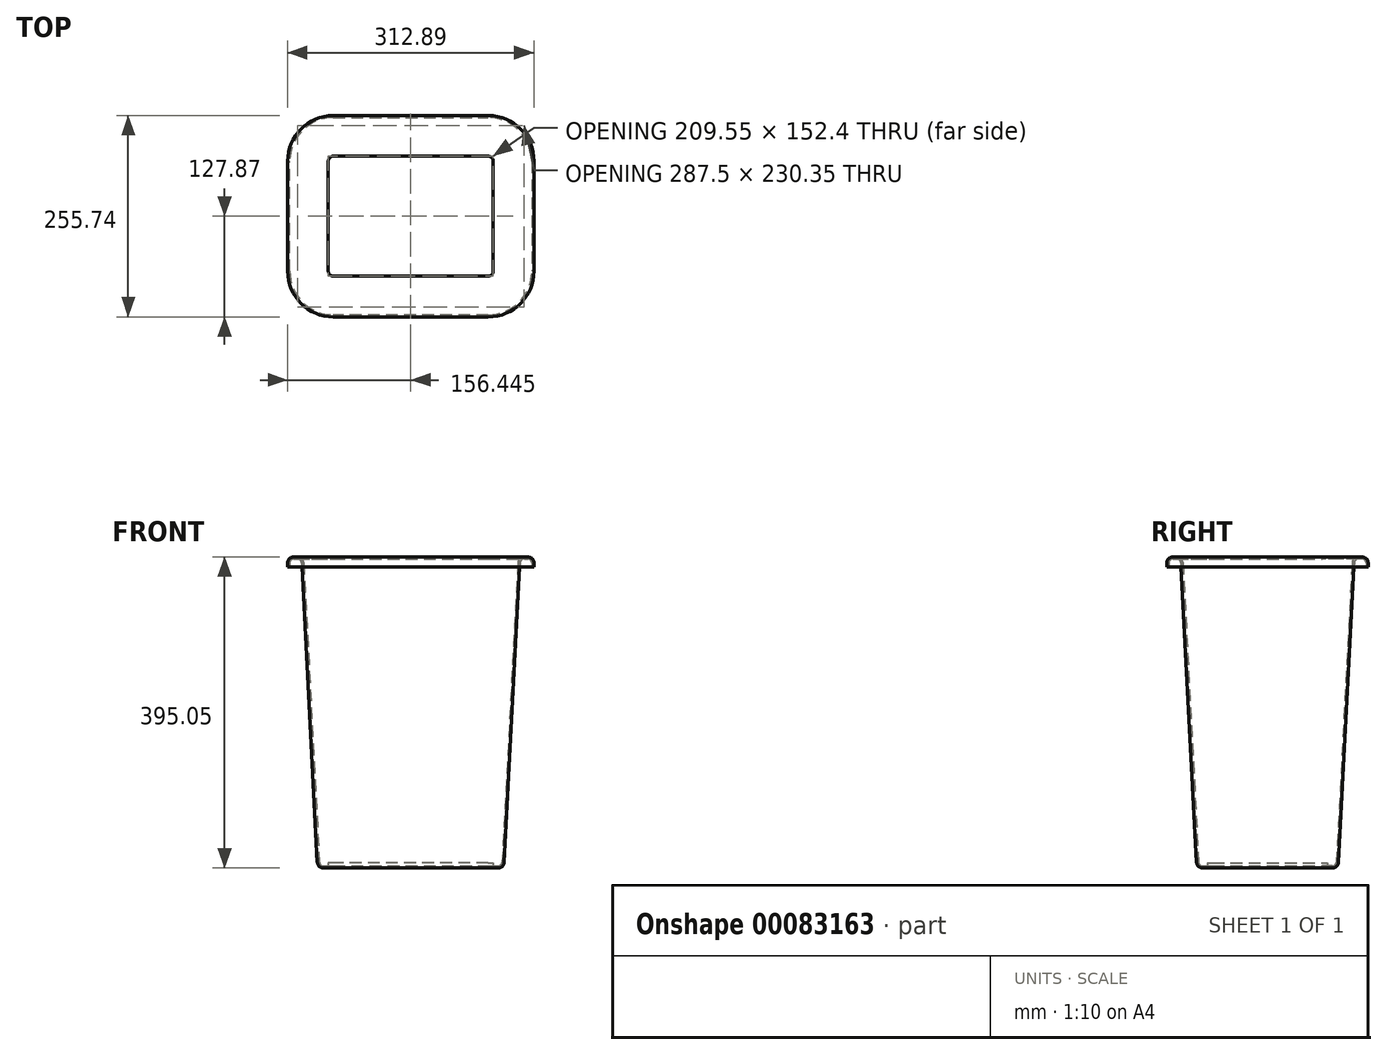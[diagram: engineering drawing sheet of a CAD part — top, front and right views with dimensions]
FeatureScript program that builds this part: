
annotation { "Feature Type Name" : "Feature", "Feature Type Description" : "" }
export const myFeature = defineFeature(function(context is Context, id is Id, definition is map)
    precondition{}
    {
        {
            var Q0;
            Q0=qCreatedBy(makeId("Front.planeOp"),FACE);
            var sketch = newSketch(context, id + "F0", { "sketchPlane" : qUnion([Q0])});
            skLineSegment(sketch, "E0", {"start": v(0, 2.54) * mm, "end": v(6.35, 2.54) * mm});
            skArc(sketch, "E1", {"start": v(6.35, 2.54) * mm, "mid": v(9.85, 3.94) * mm, "end": v(11.42, 7.35) * mm});
            skLineSegment(sketch, "E2", {"start": v(31.36, 387.83) * mm, "end": v(11.42, 7.35) * mm});
            skLineSegment(sketch, "E3.1", {"start": v(33.9, 387.7) * mm, "end": v(13.96, 7.22) * mm});
            skArc(sketch, "E3.2", {"start": v(6.35, 0) * mm, "mid": v(11.6, 2.1) * mm, "end": v(13.96, 7.22) * mm});
            skLineSegment(sketch, "E3.3", {"start": v(0, 0) * mm, "end": v(6.35, 0) * mm});
            skLineSegment(sketch, "E4", {"start": v(0, 2.54) * mm, "end": v(0, 0) * mm});
            skLineSegment(sketch, "E5", {"start": v(11.42, 7.35) * mm, "end": v(11.42, 68.2) * mm, "construction": true});
            skArc(sketch, "E6", {"start": v(33.9, 387.7) * mm, "mid": v(35.48, 391.12) * mm, "end": v(38.97, 392.51) * mm});
            skArc(sketch, "E7", {"start": v(31.36, 387.83) * mm, "mid": v(33.73, 392.96) * mm, "end": v(38.97, 395.05) * mm});
            skLineSegment(sketch, "E8", {"start": v(38.97, 395.05) * mm, "end": v(44.05, 395.05) * mm});
            skLineSegment(sketch, "E9", {"start": v(38.97, 392.51) * mm, "end": v(44.05, 392.51) * mm});
            skArc(sketch, "E10", {"start": v(44.05, 395.05) * mm, "mid": v(49.44, 392.82) * mm, "end": v(51.67, 387.43) * mm});
            skArc(sketch, "E11", {"start": v(44.05, 392.51) * mm, "mid": v(47.64, 391.03) * mm, "end": v(49.13, 387.43) * mm});
            skLineSegment(sketch, "E12", {"start": v(49.13, 387.43) * mm, "end": v(49.13, 382.35) * mm});
            skLineSegment(sketch, "E13", {"start": v(51.67, 387.43) * mm, "end": v(51.67, 382.35) * mm});
            skLineSegment(sketch, "E14", {"start": v(51.67, 382.35) * mm, "end": v(49.13, 382.35) * mm});
            skSolve(sketch);
        }
        {
            var Q0;
            Q0=qCreatedBy(makeId("Top.planeOp"),FACE);
            var sketch = newSketch(context, id + "F1", { "sketchPlane" : qUnion([Q0])});
            skLineSegment(sketch, "E15", {"start": v(0, -139.7) * mm, "end": v(0, 0) * mm});
            skArc(sketch, "E16", {"start": v(0, 0) * mm, "mid": v(-1.86, 4.5) * mm, "end": v(-6.35, 6.35) * mm});
            skLineSegment(sketch, "E17", {"start": v(-6.35, 6.35) * mm, "end": v(-203.2, 6.35) * mm});
            skArc(sketch, "E18", {"start": v(-203.2, 6.35) * mm, "mid": v(-207.7, 4.5) * mm, "end": v(-209.55, 0) * mm});
            skLineSegment(sketch, "E19", {"start": v(-209.55, 0) * mm, "end": v(-209.55, -139.7) * mm});
            skArc(sketch, "E20", {"start": v(-209.55, -139.7) * mm, "mid": v(-207.7, -144.2) * mm, "end": v(-203.2, -146.05) * mm});
            skLineSegment(sketch, "E21", {"start": v(-203.2, -146.05) * mm, "end": v(-6.35, -146.05) * mm});
            skArc(sketch, "E22", {"start": v(-6.35, -146.05) * mm, "mid": v(-1.86, -144.2) * mm, "end": v(0, -139.7) * mm});
            skSolve(sketch);
        }
        {
            var Q0;
            Q0 = qSketchRegion(id + "F0", true);
            var Q1;
            Q1 = qBodyType(qCreatedBy(id + "F1" ,EDGE), BodyType.WIRE);
            sweep(context, id + "F2", {"profiles" : qUnion([Q0]), "path" : qUnion([Q1])});
        }
        {
            var Q0;
            Q0=makeQuery(id+"F1.imprint","IMPRINT",FACE,{"disambiguationData":[TD([[makeQuery(id+"F1.imprint","IMPRINT",EDGE,{"derivedFrom":sQuery(id+"F1.wireOp",EDGE,"E15")}),1.0]])]});
            extrude(context, id + "F3", {"entities" : qUnion([Q0]), "depth" : 6.35 * mm});
        }
    });
